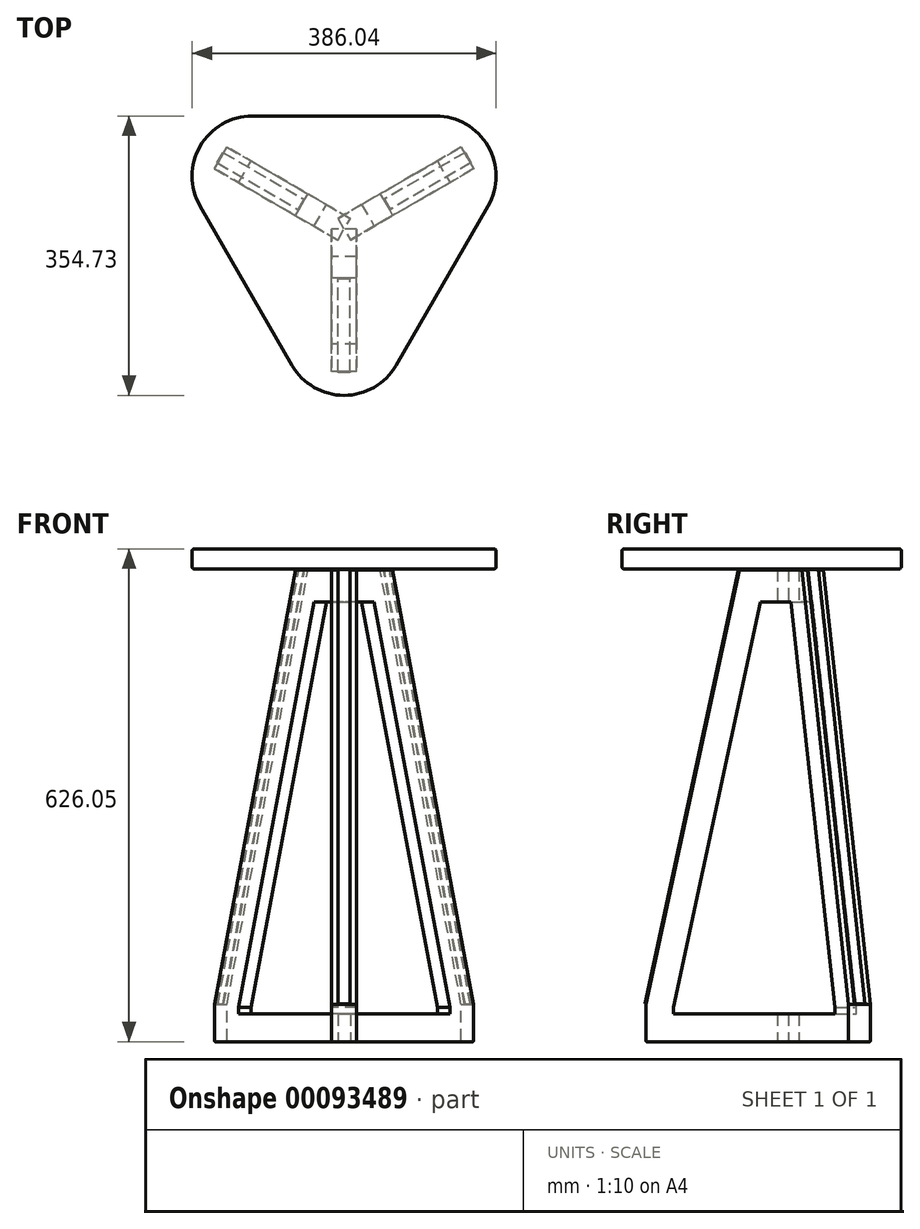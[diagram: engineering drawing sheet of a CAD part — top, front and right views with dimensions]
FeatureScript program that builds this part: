
annotation { "Feature Type Name" : "Feature", "Feature Type Description" : "" }
export const myFeature = defineFeature(function(context is Context, id is Id, definition is map)
    precondition{}
    {
        {
            var Q0;
            Q0=qCreatedBy(makeId("Top.planeOp"),FACE);
            var sketch = newSketch(context, id + "F0", { "sketchPlane" : qUnion([Q0])});
            skCircle(sketch, "E0.cCircle", {"center": v(0, 0) * mm, "radius": 287.29 * mm, "construction": true});
            skLineSegment(sketch, "E0.0", {"start": v(0, -287.29) * mm, "end": v(-248.8, 143.64) * mm});
            skLineSegment(sketch, "E0.1", {"start": v(-248.8, 143.64) * mm, "end": v(248.8, 143.64) * mm});
            skLineSegment(sketch, "E0.2", {"start": v(248.8, 143.64) * mm, "end": v(0, -287.29) * mm});
            skSolve(sketch);
        }
        {
            var Q0;
            Q0=makeQuery(id+"F0.imprint","IMPRINT",FACE,{"disambiguationData":[TD([[makeQuery(id+"F0.imprint","IMPRINT",EDGE,{"derivedFrom":sQuery(id+"F0.wireOp",EDGE,"E0.0")}),-1.0]])]});
            extrude(context, id + "F1", {"entities" : qUnion([Q0]), "endBound" : BoundingType.SYMMETRIC, "depth" : 25.4 * mm});
        }
        {
            var Q0;
            Q0=makeQuery(id+"F1.opExtrude","SWEPT_EDGE",EDGE,{"disambiguationData":[OSD([sQuery(id+"F0.wireOp",EDGE,"E0.0"),sQuery(id+"F0.wireOp",EDGE,"E0.2")])]});
            var Q1;
            Q1=makeQuery(id+"F1.opExtrude","SWEPT_EDGE",EDGE,{"disambiguationData":[OSD([sQuery(id+"F0.wireOp",EDGE,"E0.1"),sQuery(id+"F0.wireOp",EDGE,"E0.2")])]});
            var Q2;
            Q2=makeQuery(id+"F1.opExtrude","SWEPT_EDGE",EDGE,{"disambiguationData":[OSD([sQuery(id+"F0.wireOp",EDGE,"E0.0"),sQuery(id+"F0.wireOp",EDGE,"E0.1")])]});
            fillet(context, id + "F2", {"entities" : qUnion([Q0, Q1, Q2]), "radius" : 76.2 * mm, "tangentPropagation" : true, "allowEdgeOverflow" : false});
        }
        {
            var Q0;
            Q0=makeQuery(id+"F1.opExtrude","CAP_FACE",FACE,{"disambiguationData":[OSD([sQuery(id+"F0.wireOp",EDGE,"E0.0"),sQuery(id+"F0.wireOp",EDGE,"E0.1"),sQuery(id+"F0.wireOp",EDGE,"E0.2")])],"isStart":false});
            var Q1;
            Q1=makeQuery(id+"F1.opExtrude","CAP_FACE",FACE,{"disambiguationData":[OSD([sQuery(id+"F0.wireOp",EDGE,"E0.0"),sQuery(id+"F0.wireOp",EDGE,"E0.1"),sQuery(id+"F0.wireOp",EDGE,"E0.2")])],"isStart":true});
            fillet(context, id + "F3", {"entities" : qUnion([Q0, Q1]), "radius" : 2.54 * mm, "tangentPropagation" : true, "allowEdgeOverflow" : false});
        }
        {
            var Q0;
            Q0=qCreatedBy(makeId("Right.planeOp"),FACE);
            var sketch = newSketch(context, id + "F4", { "sketchPlane" : qUnion([Q0])});
            skLineSegment(sketch, "E1", {"start": v(0, -613.35) * mm, "end": v(-179.63, -613.35) * mm});
            skLineSegment(sketch, "E2", {"start": v(-180.9, -612.08) * mm, "end": v(-180.9, -565.89) * mm});
            skLineSegment(sketch, "E3", {"start": v(-180.9, -565.89) * mm, "end": v(-62.15, -14.04) * mm});
            skLineSegment(sketch, "E4", {"start": v(-62.15, -14.04) * mm, "end": v(0, -14.04) * mm});
            skLineSegment(sketch, "E5.0", {"start": v(-145.87, -569.61) * mm, "end": v(-35.03, -54.55) * mm});
            skLineSegment(sketch, "E5.1", {"start": v(-145.87, -578.32) * mm, "end": v(-145.87, -569.61) * mm});
            skLineSegment(sketch, "E5.2", {"start": v(0, -578.32) * mm, "end": v(-145.87, -578.32) * mm});
            skLineSegment(sketch, "E6", {"start": v(-35.03, -54.55) * mm, "end": v(0, -54.55) * mm});
            skLineSegment(sketch, "E7", {"start": v(0, -14.04) * mm, "end": v(0, -54.55) * mm});
            skLineSegment(sketch, "E8", {"start": v(0, -578.32) * mm, "end": v(0, -613.35) * mm});
            skPoint(sketch, "E9.visualSharp", {"position": v(-180.9, -613.35) * mm});
            skArc(sketch, "E9.filletArc", {"start": v(-180.9, -612.08) * mm, "mid": v(-180.53, -612.98) * mm, "end": v(-179.63, -613.35) * mm});
            skSolve(sketch);
        }
        {
            var Q0;
            Q0 = qSketchRegion(id + "F4", true);
            extrude(context, id + "F5", {"entities" : qUnion([Q0]), "operationType" : NewBodyOperationType.ADD, "endBound" : BoundingType.SYMMETRIC, "depth" : 31.75 * mm});
        }
        {
            var Q0;
            Q0=makeQuery(id+"F5.opExtrude","SWEPT_FACE",FACE,{"disambiguationData":[OSD([sQuery(id+"F4.wireOp",EDGE,"E3")])]});
            var sketch = newSketch(context, id + "F6", { "sketchPlane" : qUnion([Q0])});
            skLineSegment(sketch, "E10.bottom", {"start": v(7.5, -591.55) * mm, "end": v(-7.5, -591.55) * mm});
            skLineSegment(sketch, "E10.top", {"start": v(7.5, -26.53) * mm, "end": v(-7.5, -26.53) * mm});
            skLineSegment(sketch, "E10.left", {"start": v(7.5, -591.55) * mm, "end": v(7.5, -26.53) * mm});
            skLineSegment(sketch, "E10.right", {"start": v(-7.5, -591.55) * mm, "end": v(-7.5, -26.53) * mm});
            skPoint(sketch, "E10.middle", {"position": v(0, -309.04) * mm});
            skPoint(sketch, "E10.middle.positionSnap0", {"position": v(-15.88, -309.04) * mm});
            skSolve(sketch);
        }
        {
            var Q0;
            {var subQ0=sQuery(id+"F6.wireOp",EDGE,"E10.left");var subQ1=sQuery(id+"F4.wireOp",EDGE,"E3");var subQ2=makeQuery(id+"F5.opExtrude","SWEPT_EDGE",EDGE,{"disambiguationData":[OSD([sQuery(id+"F4.wireOp",EDGE,"E2"),subQ1])]});var subQ3=makeQuery(id+"F6.imprint","INTERSECT",VERTEX,{"derivedFrom":[subQ2,subQ0]});Q0=makeQuery(id+"F6.imprint","IMPRINT",FACE,{"disambiguationData":[TD([[makeQuery(id+"F6.imprint","IMPRINT",EDGE,{"disambiguationData":[TD([[subQ3,-1.0]])],"derivedFrom":subQ0}),1.0]])]});}
            extrude(context, id + "F7", {"entities" : qUnion([Q0]), "operationType" : NewBodyOperationType.ADD, "endBound" : BoundingType.SYMMETRIC, "oppositeDirection" : true, "depth" : 2.54 * mm});
        }
        {
            var Q0;
            Q0=makeQuery(id+"F5.opExtrude","SWEPT_FACE",FACE,{"disambiguationData":[OSD([sQuery(id+"F4.wireOp",EDGE,"E7")])]});
            var sketch = newSketch(context, id + "F8", { "sketchPlane" : qUnion([Q0])});
            skLineSegment(sketch, "E11", {"start": v(0, -14.04) * mm, "end": v(0, -54.55) * mm});
            skSolve(sketch);
        }
        {
            var Q0;
            Q0=makeQuery(id+"F5.opExtrude","SWEPT_BODY",BODY,{"disambiguationData":[OSD([sQuery(id+"F4.wireOp",EDGE,"E1"),sQuery(id+"F4.wireOp",EDGE,"E2"),sQuery(id+"F4.wireOp",EDGE,"E3"),sQuery(id+"F4.wireOp",EDGE,"E4"),sQuery(id+"F4.wireOp",EDGE,"E5.0"),sQuery(id+"F4.wireOp",EDGE,"E5.1"),sQuery(id+"F4.wireOp",EDGE,"E5.2"),sQuery(id+"F4.wireOp",EDGE,"E6"),sQuery(id+"F4.wireOp",EDGE,"E7"),sQuery(id+"F4.wireOp",EDGE,"E8"),sQuery(id+"F4.wireOp",EDGE,"E9.filletArc")])]});
            var Q1;
            Q1=sQuery(id+"F8.wireOp",EDGE,"E11");
            circularPattern(context, id + "F9", {"entities" : qUnion([Q0]), "axis" : qUnion([Q1]), "angle" : 360 * degree, "instanceCount" : 3, "equalSpace" : true});
        }
    });
